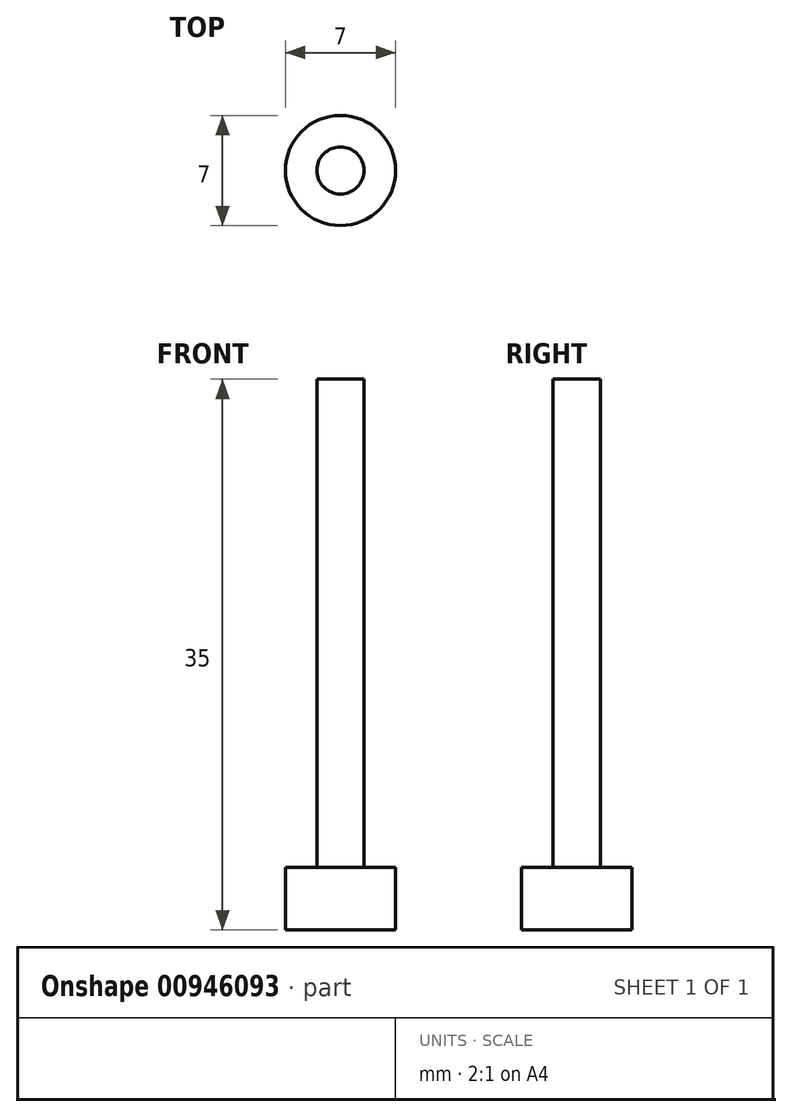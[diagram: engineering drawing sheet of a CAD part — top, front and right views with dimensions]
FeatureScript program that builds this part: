
annotation { "Feature Type Name" : "Feature", "Feature Type Description" : "" }
export const myFeature = defineFeature(function(context is Context, id is Id, definition is map)
    precondition{}
    {
        {
            var Q0;
            Q0=qCreatedBy(makeId("Top.planeOp"),FACE);
            var sketch = newSketch(context, id + "F0", { "sketchPlane" : qUnion([Q0])});
            skCircle(sketch, "E0", {"center": v(0, 0) * mm, "radius": 1.5 * mm});
            skCircle(sketch, "E1", {"center": v(0, 0) * mm, "radius": 3.5 * mm});
            skSolve(sketch);
        }
        {
            var Q0;
            Q0=makeQuery(id+"F0.imprint","IMPRINT",FACE,{"disambiguationData":[TD([[makeQuery(id+"F0.imprint","IMPRINT",EDGE,{"derivedFrom":sQuery(id+"F0.wireOp",EDGE,"E0")}),1.0]])]});
            extrude(context, id + "F1", {"entities" : qUnion([Q0]), "depth" : 35 * mm, "offsetDistance" : 25 * mm});
        }
        {
            var Q0;
            Q0=makeQuery(id+"F0.imprint","IMPRINT",FACE,{"disambiguationData":[TD([[makeQuery(id+"F0.imprint","IMPRINT",EDGE,{"derivedFrom":sQuery(id+"F0.wireOp",EDGE,"E0")}),-1.0]])]});
            var Q1;
            Q1=makeQuery(id+"F0.imprint","IMPRINT",FACE,{"disambiguationData":[TD([[makeQuery(id+"F0.imprint","IMPRINT",EDGE,{"derivedFrom":sQuery(id+"F0.wireOp",EDGE,"hGVf1BVx-XnXH-pVU1-KdR6-MI1aZuLdzy8C")}),1.0]])]});
            extrude(context, id + "F2", {"entities" : qUnion([Q0, Q1]), "operationType" : NewBodyOperationType.ADD, "depth" : 4 * mm, "offsetDistance" : 25 * mm});
        }
    });
